# Revit family: 94722221
name_source: partatom
category: Equipamento especial
revit_build: Autodesk Revit 2016 (Build: 20150220_1215(x64)
units: mm (PartAtom-declared; Revit-internal decimal feet)

## family parameters
Com base no plano de trabalho = Não
Compartilhado = Não
Corte com vazios quando carregados = Não
Cota do conector redondo = Utilizar diâmetro
Ponto de cálculo do ambiente = Não
Sempre na vertical = Sim
Tipo de parte = Normal

## types (1)
- Tramontina TDC - 94722221
    Código de montagem = 94722/221
    Descrição = New Slim Lune Touch 4EI 90 - 94722/221
    Desenvolvedor = Factory Cursos & Desenvolvimento
    Eficiência Energética = A
    Fabricante = Tramontina
    Frequência = 50 - 60 Hz
    Modelo = New Slim Lune Touch 4EI 90 - 94722/221
    Nicho para corte de instalação = 875X335 mm
    Potencia Elétrica das Areas de Aquecimento = (160mm , 200mm)=(1.4 , 2,3)kW
    Potência Elétruca total = 7,4 kW
    Site do desenvolvedor = www.factorycursos.com.br
    Tensão = 220 V
    Tipo de imagem = <Nenhum>
    URL = www.tramontina.com.br
